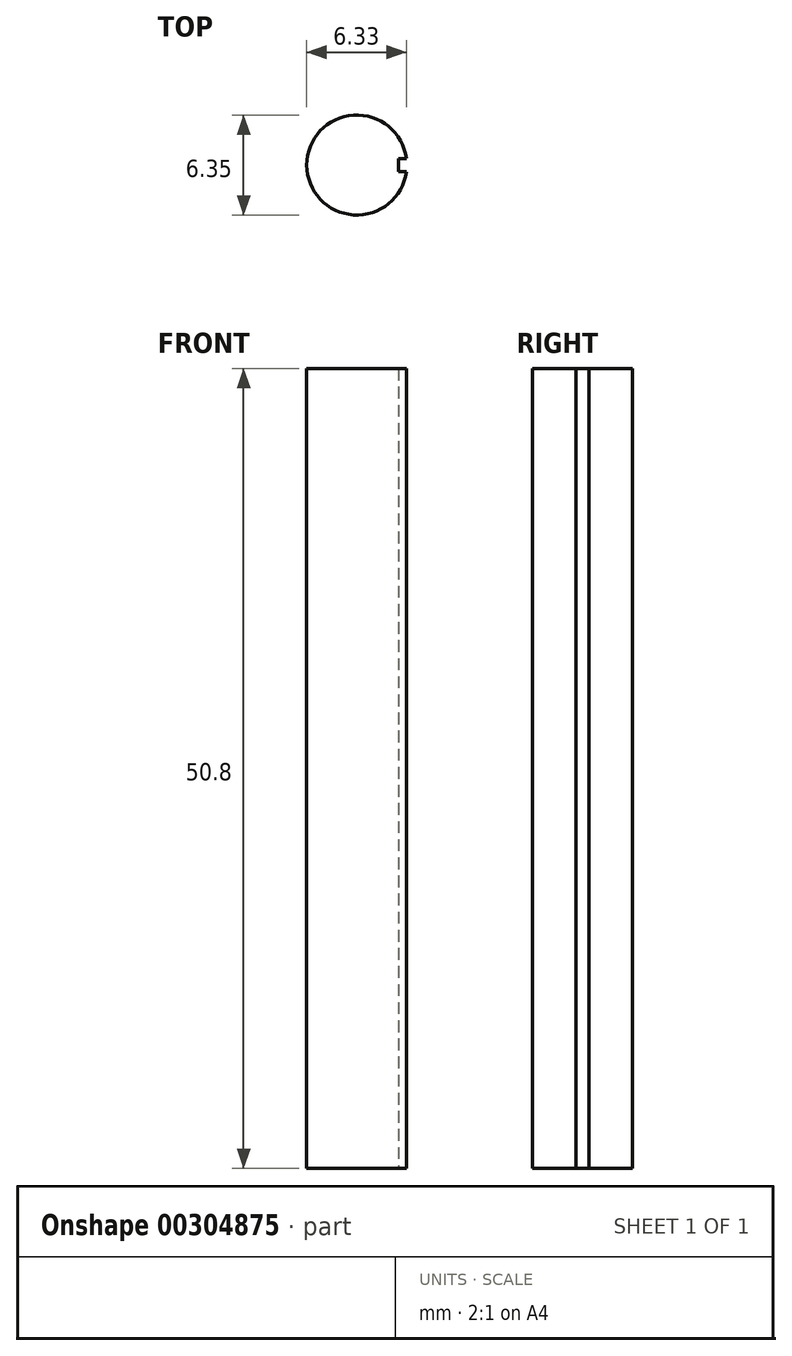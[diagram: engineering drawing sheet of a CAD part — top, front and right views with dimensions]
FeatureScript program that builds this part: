
annotation { "Feature Type Name" : "Feature", "Feature Type Description" : "" }
export const myFeature = defineFeature(function(context is Context, id is Id, definition is map)
    precondition{}
    {
        {
            var Q0;
            Q0=qCreatedBy(makeId("Top.planeOp"),FACE);
            var sketch = newSketch(context, id + "F0", { "sketchPlane" : qUnion([Q0])});
            skArc(sketch, "E0", {"start": v(3.15, 0.42) * mm, "mid": v(-3.18, 0) * mm, "end": v(3.15, -0.42) * mm});
            skLineSegment(sketch, "E1.bottom", {"start": v(2.67, 0.42) * mm, "end": v(3.15, 0.42) * mm});
            skLineSegment(sketch, "E1.top", {"start": v(2.67, -0.42) * mm, "end": v(3.15, -0.42) * mm});
            skLineSegment(sketch, "E1.left", {"start": v(2.67, 0.42) * mm, "end": v(2.67, -0.42) * mm});
            skPoint(sketch, "E1.middle", {"position": v(3.18, 0) * mm});
            skPoint(sketch, "E1.right.start.orphan", {"position": v(3.68, 0.42) * mm});
            skPoint(sketch, "E2.orphan", {"position": v(3.68, -0.42) * mm});
            skSolve(sketch);
        }
        {
            var Q0;
            Q0=makeQuery(id+"F0.imprint","IMPRINT",FACE,{"disambiguationData":[TD([[makeQuery(id+"F0.imprint","IMPRINT",EDGE,{"derivedFrom":sQuery(id+"F0.wireOp",EDGE,"E0")}),1.0]])]});
            extrude(context, id + "F1", {"entities" : qUnion([Q0]), "depth" : 50.8 * mm});
        }
    });
